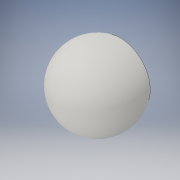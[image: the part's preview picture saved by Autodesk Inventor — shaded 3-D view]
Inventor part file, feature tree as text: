
AUTODESK INVENTOR PART (.ipt)
format: ipt  version: 2016 (Build 200138000, 138)  size: 187,392 bytes
history: native  units: in
note: dims shown in document units (in); Inventor stores cm internally (conversion verified against a paired STEP export)
features: plane x3, sketch x3, projected_geometry x2, revolve x1, extrude x1
ambient origin geometry x8: Origin, YZ Plane, XZ Plane, XY Plane, X Axis, Y Axis, Z Axis, Center Point
bodies: Solid1 (feature_tree)
feature tree (10):
  plane  "Work Plane1"
  sketch  "Sketch3"  dims[d11=180.0deg d12=0.0984in d13=0.0in]
  plane  "Work Plane2"
  sketch  "Sketch5"
  revolve  "Revolution2"  [1 undecoded]
  plane  "Work Plane3"
  extrude  "Extrusion2"  [1 undecoded]
  projected_geometry  "Projected Loop2"
  sketch  "Sketch6"
  projected_geometry  "Projected Loop3"
note: 2 required parameter values undecoded (feature->parameter linkage not recoverable at this tier; creation-order binding heuristic only, values carry confidence <= 0.55)